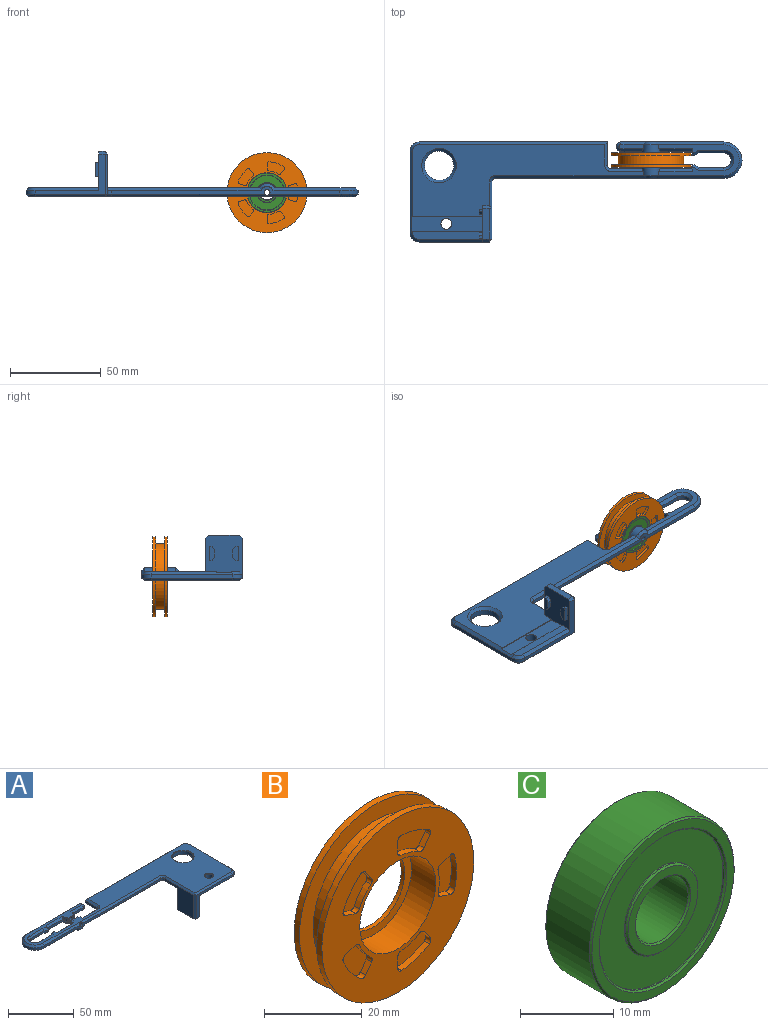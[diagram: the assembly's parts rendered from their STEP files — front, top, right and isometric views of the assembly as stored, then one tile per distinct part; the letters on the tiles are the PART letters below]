
ASSEMBLY  parts=3 mates=3
PART A: 130 faces, bbox 182.6x55.1x25.1 mm
  f0: plane 126.82x39.5mm, normal (0,0,-1), area 2484.6mm2, adj f13,f34,f51,f55,f80,f82,f84,f107
  f1: plane 13.49x2.25mm, normal (0,0,-1), area 29.8mm2, adj f53,f71,f72,f73
  f2: cylinder r=3.75mm len=7.5mm, axis (0,1,0), area 24.9mm2, adj f4,f54,f65
  f3: plane 56.54x4.25mm, normal (0,1,0), area 117.1mm2, adj f17,f57,f61,f73,f74,f75,f92
  f4: plane 179.5x52mm, normal (0,0,1), area 3439.6mm2, adj f2,f6,f19,f27,f53,f54,f55,f56
  f5: plane 44.32x17mm, normal (0,0,-1), area 259.1mm2, adj f19,f27,f53,f55,f75,f76,f77,f113
  f6: cylinder r=3.75mm len=7.5mm, axis (0,1,0), area 24.9mm2, adj f4,f56,f68
  f7: plane 17.91x2mm, normal (0,-1,0), area 35.6mm2, adj f27,f53,f126,f128
  f8: plane 11.7x2mm, normal (0,-1,0), area 23.2mm2, adj f53,f57,f71,f85
  f9: plane 17.91x2mm, normal (0,1,0), area 35.6mm2, adj f19,f55,f125,f127
  f10: plane 38.5x4.5mm, normal (0,0,-1), area 170.6mm2, adj f13,f50,f105,f106,f107
  f11: plane 45x2mm, normal (1,0,0), area 90mm2, adj f15,f32,f93,f107
  f12: cylinder r=3mm len=6mm, axis (0,0,-1), area 75.4mm2, adj f52,f63
  f13: plane 21.5x20mm, normal (1,0,0), area 360.9mm2, adj f0,f10,f31,f34,f35,f36,f37,f38
  f14: plane 12.75x2mm, normal (-1,0,0), area 25.5mm2, adj f16,f60,f83,f112
  f15: cylinder r=5mm len=5mm, axis (0,0,-1), area 15.7mm2, adj f11,f16,f90,f108
  f16: plane 103.5x2mm, normal (0,1,0), area 207mm2, adj f14,f15,f86,f110
  f17: cylinder r=10mm len=20mm, axis (0,0,-1), area 62.8mm2, adj f3,f28,f76,f96
  f18: plane 17.16x2mm, normal (0,1,0), area 34.1mm2, adj f55,f60,f79,f109
  f19: plane 5x3.75mm, normal (1,0,0), area 12.3mm2, adj f4,f5,f9,f20,f116,f119,f125,f127
  f20: plane 2.96x1mm, normal (0,1,0), area 2.5mm2, adj f19,f21,f116,f119
  f21: plane 2.74x2mm, normal (-0.48,0.88,0), area 6.2mm2, adj f20,f22,f116,f119
  f22: plane 13.51x2mm, normal (0,1,0), area 27mm2, adj f21,f23,f118,f121
  f23: cylinder r=4mm len=8mm, axis (0,0,-1), area 25.1mm2, adj f22,f24,f117,f123
  f24: plane 13.51x2mm, normal (0,-1,0), area 27mm2, adj f23,f25,f115,f124
  f25: plane 2.74x2mm, normal (-0.48,-0.88,0), area 6.2mm2, adj f24,f26,f114,f122
  f26: plane 2x1mm, normal (0,-1,0), area 2mm2, adj f25,f27,f113,f120
  f27: plane 5x3.75mm, normal (1,0,0), area 11.3mm2, adj f4,f5,f7,f26,f113,f120,f126,f128
  f28: plane 125.5x4.25mm, normal (0,-1,0), area 255mm2, adj f17,f29,f62,f77,f78,f80,f99
  f29: cylinder r=2mm len=2mm, axis (0,0,-1), area 6.3mm2, adj f28,f30,f82,f102
  f30: plane 31.5x22mm, normal (-1,0,0), area 403mm2, adj f29,f84,f88,f95,f101,f104
  f31: plane 38.5x22mm, normal (0,-1,0), area 147mm2, adj f13,f32,f94,f100,f101,f105
  f32: cylinder r=5mm len=5mm, axis (0,0,-1), area 15.7mm2, adj f11,f31,f97,f106
  f33: cylinder r=8mm len=16mm, axis (0,0,-1), area 150.8mm2, adj f64,f129
  f34: plane 18.5x3.5mm, normal (0,1,0), area 64.7mm2, adj f0,f13,f87,f88
  f35: plane 17x3.5mm, normal (0,0,-1), area 59.5mm2, adj f13,f87,f94,f95
  f36: plane 2x1.5mm, normal (0,0,1), area 3mm2, adj f13,f37,f41,f42
  f37: plane 8x2mm, normal (0,-1,0), area 16mm2, adj f13,f36,f38,f42
  f38: plane 2x1.5mm, normal (0,0,-1), area 3mm2, adj f13,f37,f39,f42
  f39: plane 2x2mm, normal (0,0.8,-0.6), area 5mm2, adj f13,f38,f40,f42
  f40: plane 4x2mm, normal (0,1,0), area 8mm2, adj f13,f39,f41,f42
  f41: plane 2x2mm, normal (0,0.8,0.6), area 5mm2, adj f13,f36,f40,f42
  f42: plane 8x3mm, normal (1,0,0), area 21mm2, adj f36,f37,f38,f39,f40,f41
  f43: plane 8x2mm, normal (0,1,0), area 16mm2, adj f13,f44,f48,f49
  f44: plane 2x1.5mm, normal (0,0,1), area 3mm2, adj f13,f43,f45,f49
  f45: plane 2x2mm, normal (0,-0.8,0.6), area 5mm2, adj f13,f44,f46,f49
  f46: plane 4x2mm, normal (0,-1,0), area 8mm2, adj f13,f45,f47,f49
  f47: plane 2x2mm, normal (0,-0.8,-0.6), area 5mm2, adj f13,f46,f48,f49
  f48: plane 2x1.5mm, normal (0,0,-1), area 3mm2, adj f13,f43,f47,f49
  f49: plane 8x3mm, normal (1,0,0), area 21mm2, adj f43,f44,f45,f46,f47,f48
  f50: plane 39x0.5mm, normal (0,1,0), area 19.4mm2, adj f10,f13,f52,f107
  f51: plane 39x0.5mm, normal (0,-1,0), area 19.4mm2, adj f0,f13,f52,f107
  f52: plane 39x8mm, normal (0,0,-1), area 283.7mm2, adj f12,f13,f50,f51,f107
  f53: cylinder r=5mm len=10mm, axis (0,1,0), area 77.6mm2, adj f1,f4,f5,f7,f8,f54,f71,f74
  f54: plane 10x7.25mm, normal (0,-1,0), area 23.1mm2, adj f2,f4,f53
  f55: cylinder r=5mm len=10mm, axis (0,-1,0), area 57.2mm2, adj f0,f4,f5,f9,f18,f56,f78,f79
  f56: plane 10x7.25mm, normal (0,1,0), area 23.1mm2, adj f4,f6,f55
  f57: cylinder r=2.62mm len=5.25mm, axis (0,0,1), area 16.5mm2, adj f3,f8,f72,f89
  f58: plane 6.5x5mm, normal (0,1,0), area 13.5mm2, adj f68,f69,f70
  f59: plane 6.5x5mm, normal (0,-1,0), area 13.5mm2, adj f65,f66,f67
  f60: cylinder r=2mm len=2mm, axis (0,0,-1), area 6.3mm2, adj f14,f18,f81,f111
  f61: cylinder r=1.65mm len=8.5mm, axis (0,-1,0), area 86mm2, adj f3,f67,f92
  f62: cylinder r=1.65mm len=7.5mm, axis (0,-1,0), area 75.6mm2, adj f28,f70,f99
  f63: cone r=3mm half-angle=45deg, axis (0,0,1), area 14.4mm2, adj f4,f12
  f64: cone r=8mm half-angle=45deg, axis (0,0,1), area 36.7mm2, adj f4,f33
  f65: cone r=3.25mm half-angle=45deg, axis (0,1,0), area 10.8mm2, adj f2,f59,f66
  f66: plane 6.01x0.51mm, normal (0,-0.71,0.71), area 3.6mm2, adj f4,f59,f65,f67
  f67: cone r=1.65mm half-angle=45deg, axis (0,-1,0), area 8mm2, adj f59,f61,f66
  f68: cone r=3.75mm half-angle=45deg, axis (0,-1,0), area 10.8mm2, adj f6,f58,f69
  f69: plane 6.01x0.51mm, normal (0,0.71,0.71), area 3.6mm2, adj f4,f58,f68,f70
  f70: cone r=2.15mm half-angle=45deg, axis (0,1,0), area 8mm2, adj f58,f62,f69
  f71: plane 12.42x1.56mm, normal (0,-0.71,-0.71), area 25.4mm2, adj f1,f8,f53,f72
  f72: cone r=2.62mm half-angle=45deg, axis (0,0,1), area 12.5mm2, adj f1,f57,f71,f73
  f73: plane 13.4x1.63mm, normal (0,0.71,-0.71), area 27.2mm2, adj f1,f3,f72,f74
  f74: cone r=5mm half-angle=45deg, axis (0,-1,0), area 19.7mm2, adj f3,f53,f73,f75
  f75: plane 36.86x1.63mm, normal (0,0.71,-0.71), area 76.9mm2, adj f3,f5,f74,f76
  f76: cone r=10mm half-angle=45deg, axis (0,0,1), area 61.6mm2, adj f5,f17,f75,f77
  f77: plane 36.86x1.63mm, normal (0,-0.71,-0.71), area 76.9mm2, adj f5,f28,f76,f78
  f78: cone r=3.5mm half-angle=45deg, axis (0,1,0), area 19.7mm2, adj f28,f55,f77,f80
  f79: plane 17.57x1.54mm, normal (0,0.71,0.71), area 36.6mm2, adj f4,f18,f55,f81
  f80: plane 82.36x1.63mm, normal (0,-0.71,-0.71), area 173.4mm2, adj f0,f28,f78,f82
  f81: cone r=3.5mm half-angle=45deg, axis (0,0,1), area 9.2mm2, adj f4,f60,f79,f83
  f82: cone r=3.5mm half-angle=45deg, axis (0,0,-1), area 9.2mm2, adj f0,f29,f80,f84
  f83: plane 12.75x1.5mm, normal (-0.71,0,0.71), area 25.5mm2, adj f4,f14,f81,f86
  f84: plane 14.5x1.5mm, normal (-0.71,0,-0.71), area 29.2mm2, adj f0,f30,f82,f88
  f85: plane 12.11x1.54mm, normal (0,-0.71,0.71), area 25mm2, adj f4,f8,f53,f89
  f86: plane 103.5x1.5mm, normal (0,0.71,0.71), area 218mm2, adj f4,f16,f83,f90
  f87: plane 3.5x1.5mm, normal (0,0.71,-0.71), area 7.4mm2, adj f13,f34,f35,f91
  f88: plane 20x1.5mm, normal (-0.71,0.71,0), area 40.8mm2, adj f30,f34,f84,f91
  f89: cone r=1.12mm half-angle=45deg, axis (0,0,-1), area 12.5mm2, adj f4,f57,f85,f92
  f90: cone r=3.5mm half-angle=45deg, axis (0,0,-1), area 14.2mm2, adj f4,f15,f86,f93
  f91: plane 1.5x1.5mm, normal (-0.58,0.58,-0.58), area 1.9mm2, adj f87,f88,f95
  f92: plane 56.54x1.5mm, normal (0,0.71,0.71), area 117.3mm2, adj f3,f4,f61,f89,f96
  f93: plane 45x1.5mm, normal (0.71,0,0.71), area 95.5mm2, adj f4,f11,f90,f97
  f94: plane 3.5x1.5mm, normal (0,-0.71,-0.71), area 7.4mm2, adj f13,f31,f35,f98
  f95: plane 17x1.5mm, normal (-0.71,0,-0.71), area 36.1mm2, adj f30,f35,f91,f98
  f96: cone r=8.5mm half-angle=45deg, axis (0,0,-1), area 61.6mm2, adj f4,f17,f92,f99
  f97: cone r=3.5mm half-angle=45deg, axis (0,0,-1), area 14.2mm2, adj f4,f32,f93,f100
  f98: plane 1.5x1.5mm, normal (-0.58,-0.58,-0.58), area 1.9mm2, adj f94,f95,f101
  f99: plane 125.5x1.5mm, normal (0,-0.71,0.71), area 263.6mm2, adj f4,f28,f62,f96,f102
  f100: plane 38.5x1.5mm, normal (0,-0.71,0.71), area 81.7mm2, adj f4,f31,f97,f103
  f101: plane 22x1.5mm, normal (-0.71,-0.71,0), area 46.7mm2, adj f30,f31,f98,f103
  f102: cone r=2mm half-angle=45deg, axis (0,0,1), area 9.2mm2, adj f4,f29,f99,f104
  f103: plane 1.5x1.5mm, normal (-0.58,-0.58,0.58), area 1.9mm2, adj f100,f101,f104
  f104: plane 31.5x1.5mm, normal (-0.71,0,0.71), area 66.8mm2, adj f4,f30,f102,f103
  f105: plane 35x1.5mm, normal (0,-0.71,-0.71), area 74.2mm2, adj f10,f13,f31,f106
  f106: cone r=5mm half-angle=45deg, axis (0,0,1), area 14.2mm2, adj f10,f32,f105,f107
  f107: plane 45x1.5mm, normal (0.71,0,-0.71), area 89.8mm2, adj f0,f10,f11,f50,f51,f52,f106,f108
  f108: cone r=5mm half-angle=45deg, axis (0,0,1), area 14.2mm2, adj f0,f15,f107,f110
  f109: plane 17.88x1.56mm, normal (0,0.71,-0.71), area 37mm2, adj f0,f18,f55,f111
  f110: plane 103.5x1.5mm, normal (0,0.71,-0.71), area 218mm2, adj f0,f16,f108,f112
  f111: cone r=3.5mm half-angle=45deg, axis (0,0,-1), area 9.2mm2, adj f0,f60,f109,f112
  f112: plane 12.75x1.5mm, normal (-0.71,0,-0.71), area 25.5mm2, adj f0,f14,f110,f111
  f113: plane 1.5x1.5mm, normal (0,-0.71,-0.71), area 1.7mm2, adj f5,f26,f27,f114
  f114: plane 3.12x3mm, normal (-0.34,-0.62,-0.71), area 6.6mm2, adj f5,f25,f113,f115
  f115: plane 13.9x1.5mm, normal (0,-0.71,-0.71), area 29.1mm2, adj f5,f24,f114,f117
  f116: plane 3.74x3mm, normal (-0.34,0.62,-0.71), area 8.2mm2, adj f5,f19,f20,f21,f118
  f117: cone r=5.5mm half-angle=45deg, axis (0,0,-1), area 31.7mm2, adj f5,f23,f115,f118
  f118: plane 13.9x1.5mm, normal (0,0.71,-0.71), area 29.1mm2, adj f5,f22,f116,f117
  f119: plane 3.74x3mm, normal (-0.34,0.62,0.71), area 8.2mm2, adj f4,f19,f20,f21,f121
  f120: plane 1.5x1.5mm, normal (0,-0.71,0.71), area 1.7mm2, adj f4,f26,f27,f122
  f121: plane 13.9x1.5mm, normal (0,0.71,0.71), area 29.1mm2, adj f4,f22,f119,f123
  f122: plane 3.12x3mm, normal (-0.34,-0.62,0.71), area 6.6mm2, adj f4,f25,f120,f124
  f123: cone r=4mm half-angle=45deg, axis (0,0,1), area 31.7mm2, adj f4,f23,f121,f124
  f124: plane 13.9x1.5mm, normal (0,-0.71,0.71), area 29.1mm2, adj f4,f24,f122,f123
  f125: plane 18.63x1.56mm, normal (0,0.71,-0.71), area 38.6mm2, adj f5,f9,f19,f55
  f126: plane 18.63x1.56mm, normal (0,-0.71,-0.71), area 38.6mm2, adj f5,f7,f27,f53
  f127: plane 18.32x1.54mm, normal (0,0.71,0.71), area 38.2mm2, adj f4,f9,f19,f55
  f128: plane 18.32x1.54mm, normal (0,-0.71,0.71), area 38.2mm2, adj f4,f7,f27,f53
  f129: cone r=9.5mm half-angle=45deg, axis (0,0,-1), area 116.6mm2, adj f0,f33
PART B: 55 faces, bbox 44x8x44 mm
  f0: plane 44x44mm, normal (0,1,0), area 1266.1mm2, adj f1,f9
  f1: cylinder r=22mm len=44mm, axis (0,-1,0), area 207.3mm2, adj f0,f2
  f2: plane 44x44mm, normal (0,-1,0), area 502.7mm2, adj f1,f3
  f3: cylinder r=18mm len=36mm, axis (0,-1,0), area 565.5mm2, adj f2,f4
  f4: plane 44x44mm, normal (0,1,0), area 502.7mm2, adj f3,f5
  f5: cylinder r=22mm len=44mm, axis (0,-1,0), area 207.3mm2, adj f4,f6
  f6: plane 44x44mm, normal (0,-1,0), area 916.9mm2, adj f5,f7,f10,f11,f12,f13,f14,f15
  f7: cylinder r=11mm len=22mm, axis (0,-1,0), area 483.8mm2, adj f6,f8
  f8: plane 22x22mm, normal (0,-1,0), area 125.7mm2, adj f7,f9
  f9: cylinder r=9mm len=18mm, axis (0,-1,0), area 56.5mm2, adj f0,f8
  f10: plane 2.86x1.5mm, normal (0.31,0,0.95), area 4.5mm2, adj f6,f11,f17,f18
  f11: cylinder r=1mm len=1.5mm, axis (0,-1,0), area 2.5mm2, adj f6,f10,f12,f18
  f12: cylinder r=17mm len=8.47mm, axis (0,-1,0), area 12.8mm2, adj f6,f11,f13,f18
  f13: cylinder r=1mm len=1.5mm, axis (0,-1,0), area 2.5mm2, adj f6,f12,f14,f18
  f14: plane 2.86x1.5mm, normal (0.31,0,-0.95), area 4.5mm2, adj f6,f13,f15,f18
  f15: cylinder r=1mm len=1.5mm, axis (0,-1,0), area 2.2mm2, adj f6,f14,f16,f18
  f16: cylinder r=12mm len=5.64mm, axis (0,-1,0), area 8.5mm2, adj f6,f15,f17,f18
  f17: cylinder r=1mm len=1.5mm, axis (0,-1,0), area 2.2mm2, adj f6,f10,f16,f18
  f18: plane 9.97x5.36mm, normal (0,-1,0), area 44.7mm2, adj f10,f11,f12,f13,f14,f15,f16,f17
  f19: plane 3.01x1.5mm, normal (1,0,0), area 4.5mm2, adj f6,f20,f26,f27
  f20: cylinder r=1mm len=1.5mm, axis (0,-1,0), area 2.5mm2, adj f6,f19,f21,f27
  f21: cylinder r=17mm len=8.05mm, axis (0,-1,0), area 12.8mm2, adj f6,f20,f22,f27
  f22: cylinder r=1mm len=1.5mm, axis (0,-1,0), area 2.5mm2, adj f6,f21,f23,f27
  f23: plane 2.43x1.77mm, normal (-0.81,0,-0.59), area 4.5mm2, adj f6,f22,f24,f27
  f24: cylinder r=1mm len=1.5mm, axis (0,-1,0), area 2.2mm2, adj f6,f23,f25,f27
  f25: cylinder r=12mm len=5.36mm, axis (0,-1,0), area 8.5mm2, adj f6,f24,f26,f27
  f26: cylinder r=1mm len=1.5mm, axis (0,-1,0), area 2.2mm2, adj f6,f19,f25,f27
  f27: plane 9.58x6.9mm, normal (0,-1,0), area 44.7mm2, adj f19,f20,f21,f22,f23,f24,f25,f26
  f28: plane 2.86x1.5mm, normal (0.31,0,-0.95), area 4.5mm2, adj f6,f29,f35,f36
  f29: cylinder r=1mm len=1.5mm, axis (0,-1,0), area 2.5mm2, adj f6,f28,f30,f36
  f30: cylinder r=17mm len=6.85mm, axis (0,-1,0), area 12.8mm2, adj f6,f29,f31,f36
  f31: cylinder r=1mm len=1.5mm, axis (0,-1,0), area 2.5mm2, adj f6,f30,f32,f36
  f32: plane 2.43x1.77mm, normal (-0.81,0,0.59), area 4.5mm2, adj f6,f31,f33,f36
  f33: cylinder r=1mm len=1.5mm, axis (0,-1,0), area 2.2mm2, adj f6,f32,f34,f36
  f34: cylinder r=12mm len=4.56mm, axis (0,-1,0), area 8.5mm2, adj f6,f33,f35,f36
  f35: cylinder r=1mm len=1.5mm, axis (0,-1,0), area 2.2mm2, adj f6,f28,f34,f36
  f36: plane 9.38x8.45mm, normal (0,-1,0), area 44.7mm2, adj f28,f29,f30,f31,f32,f33,f34,f35
  f37: plane 2.43x1.77mm, normal (-0.81,0,-0.59), area 4.5mm2, adj f6,f38,f44,f45
  f38: cylinder r=1mm len=1.5mm, axis (0,-1,0), area 2.5mm2, adj f6,f37,f39,f45
  f39: cylinder r=17mm len=6.85mm, axis (0,-1,0), area 12.8mm2, adj f6,f38,f40,f45
  f40: cylinder r=1mm len=1.5mm, axis (0,-1,0), area 2.5mm2, adj f6,f39,f41,f45
  f41: plane 2.86x1.5mm, normal (0.31,0,0.95), area 4.5mm2, adj f6,f40,f42,f45
  f42: cylinder r=1mm len=1.5mm, axis (0,-1,0), area 2.2mm2, adj f6,f41,f43,f45
  f43: cylinder r=12mm len=4.56mm, axis (0,-1,0), area 8.5mm2, adj f6,f42,f44,f45
  f44: cylinder r=1mm len=1.5mm, axis (0,-1,0), area 2.2mm2, adj f6,f37,f43,f45
  f45: plane 9.38x8.45mm, normal (0,-1,0), area 44.7mm2, adj f37,f38,f39,f40,f41,f42,f43,f44
  f46: plane 2.43x1.77mm, normal (-0.81,0,0.59), area 4.5mm2, adj f6,f47,f53,f54
  f47: cylinder r=1mm len=1.5mm, axis (0,-1,0), area 2.5mm2, adj f6,f46,f48,f54
  f48: cylinder r=17mm len=8.05mm, axis (0,-1,0), area 12.8mm2, adj f6,f47,f49,f54
  f49: cylinder r=1mm len=1.5mm, axis (0,-1,0), area 2.5mm2, adj f6,f48,f50,f54
  f50: plane 3.01x1.5mm, normal (1,0,0), area 4.5mm2, adj f6,f49,f51,f54
  f51: cylinder r=1mm len=1.5mm, axis (0,-1,0), area 2.2mm2, adj f6,f50,f52,f54
  f52: cylinder r=12mm len=5.36mm, axis (0,-1,0), area 8.5mm2, adj f6,f51,f53,f54
  f53: cylinder r=1mm len=1.5mm, axis (0,-1,0), area 2.2mm2, adj f6,f46,f52,f54
  f54: plane 9.58x6.9mm, normal (0,-1,0), area 44.7mm2, adj f46,f47,f48,f49,f50,f51,f52,f53
PART C: 20 faces, bbox 22x7x22 mm
  f0: plane 21.6x21.6mm, normal (0,-1,0), area 70.8mm2, adj f18,f19
  f1: cylinder r=9.5mm len=19mm, axis (0,-1,0), area 11.9mm2, adj f2,f19
  f2: plane 19x19mm, normal (0,-1,0), area 188.5mm2, adj f1,f3
  f3: cylinder r=5.5mm len=11mm, axis (0,-1,0), area 6.9mm2, adj f2,f13
  f4: plane 10.6x10.6mm, normal (0,-1,0), area 32.8mm2, adj f12,f13
  f5: cylinder r=4mm len=8mm, axis (0,-1,0), area 165.9mm2, adj f12,f14
  f6: plane 10.6x10.6mm, normal (0,1,0), area 32.8mm2, adj f14,f15
  f7: cylinder r=5.5mm len=11mm, axis (0,-1,0), area 6.9mm2, adj f8,f15
  f8: plane 19x19mm, normal (0,1,0), area 188.5mm2, adj f7,f9
  f9: cylinder r=9.5mm len=19mm, axis (0,-1,0), area 11.9mm2, adj f8,f16
  f10: plane 21.6x21.6mm, normal (0,1,0), area 70.8mm2, adj f16,f17
  f11: cylinder r=11mm len=22mm, axis (0,-1,0), area 456.2mm2, adj f17,f18
  f12: cone r=4mm half-angle=45deg, axis (0,-1,0), area 7.3mm2, adj f4,f5
  f13: cone r=5.3mm half-angle=45deg, axis (0,1,0), area 9.6mm2, adj f3,f4
  f14: cone r=4.2mm half-angle=45deg, axis (0,1,0), area 7.3mm2, adj f5,f6
  f15: cone r=5.5mm half-angle=45deg, axis (0,-1,0), area 9.6mm2, adj f6,f7
  f16: cone r=9.7mm half-angle=45deg, axis (0,1,0), area 17.1mm2, adj f9,f10
  f17: cone r=11mm half-angle=45deg, axis (0,-1,0), area 19.4mm2, adj f10,f11
  f18: cone r=10.8mm half-angle=45deg, axis (0,1,0), area 19.4mm2, adj f0,f11
  f19: cone r=9.5mm half-angle=45deg, axis (0,-1,0), area 17.1mm2, adj f0,f1
PLACE A rot(axis=(0,-1,0),180deg) t=(-140.94,4.23,9.17)mm
PLACE B t=(-30.94,17.73,6.42)mm
PLACE C t=(-30.94,21.23,6.42)mm
MATE cylindrical A.f2 <-> C.f1  axis (0,1,0) through (-30.94,24.73,6.42)mm
MATE fastened C.f1 <-> B.f1  axis (0,1,0) through (-30.94,24.73,6.42)mm
MATE planar C.f1 <-> A.f54  axis (0,1,0) through (-30.94,24.73,6.42)mm
